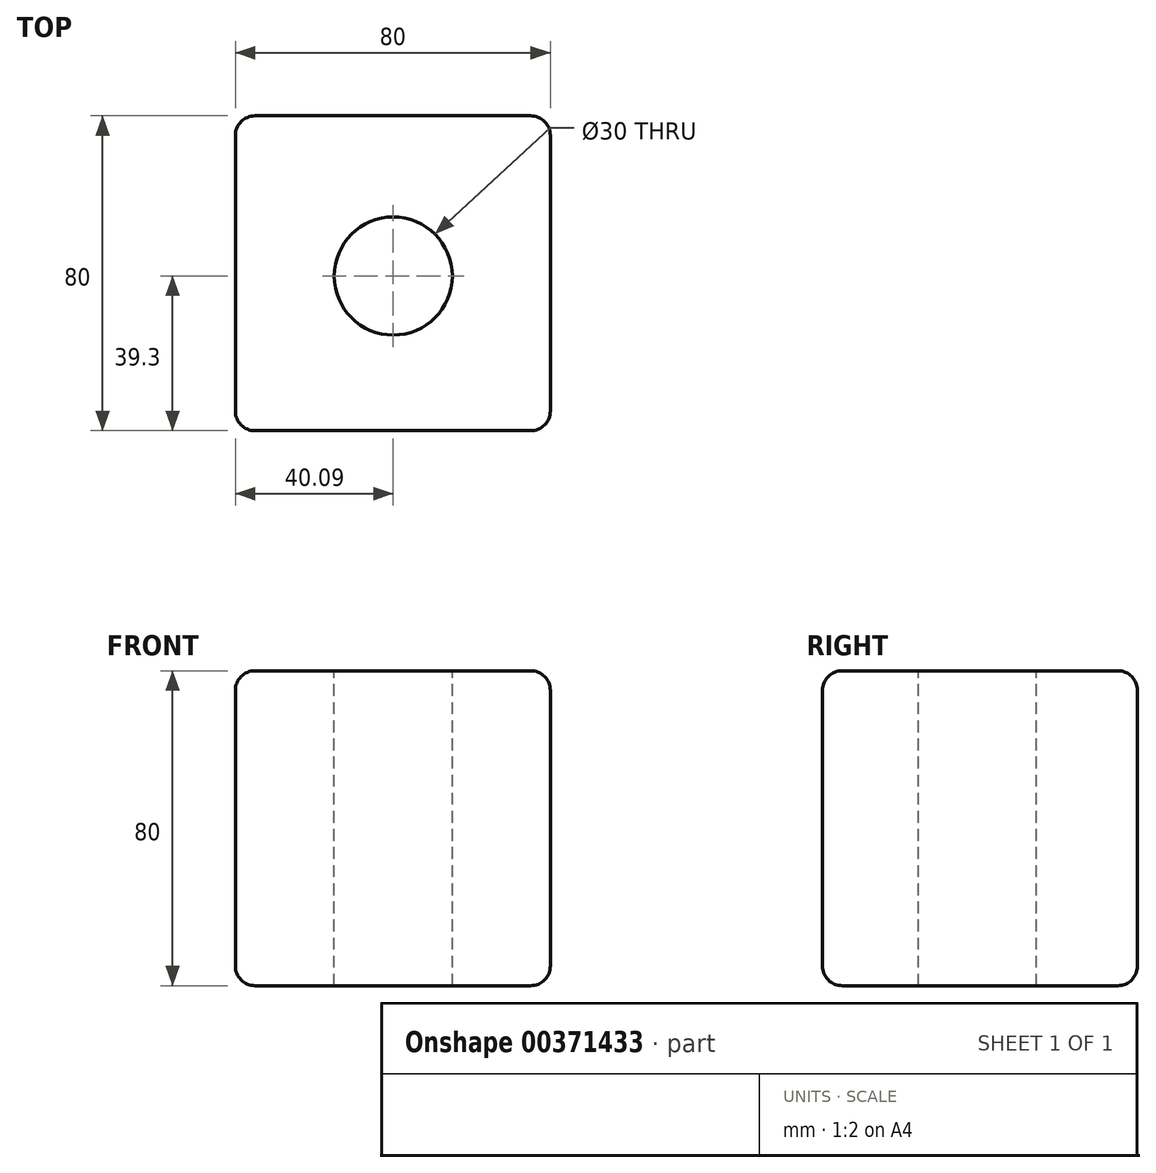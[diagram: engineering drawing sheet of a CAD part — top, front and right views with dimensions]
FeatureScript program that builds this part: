
annotation { "Feature Type Name" : "Feature", "Feature Type Description" : "" }
export const myFeature = defineFeature(function(context is Context, id is Id, definition is map)
    precondition{}
    {
        {
            var Q0;
            Q0=qCreatedBy(makeId("Top.planeOp"),FACE);
            var sketch = newSketch(context, id + "F0", { "sketchPlane" : qUnion([Q0])});
            skLineSegment(sketch, "E0.bottom", {"start": v(-46.4, 36.65) * mm, "end": v(33.6, 36.65) * mm});
            skLineSegment(sketch, "E0.top", {"start": v(-46.4, -43.35) * mm, "end": v(33.6, -43.35) * mm});
            skLineSegment(sketch, "E0.left", {"start": v(-46.4, 36.65) * mm, "end": v(-46.4, -43.35) * mm});
            skLineSegment(sketch, "E0.right", {"start": v(33.6, 36.65) * mm, "end": v(33.6, -43.35) * mm});
            skSolve(sketch);
        }
        {
            var Q0;
            Q0=makeQuery(id+"F0.imprint","IMPRINT",FACE,{"disambiguationData":[TD([[makeQuery(id+"F0.imprint","IMPRINT",EDGE,{"derivedFrom":sQuery(id+"F0.wireOp",EDGE,"E0.bottom")}),-1.0]])]});
            extrude(context, id + "F1", {"entities" : qUnion([Q0]), "depth" : 80 * mm});
        }
        {
            var Q0;
            Q0=makeQuery(id+"F1.opExtrude","CAP_FACE",FACE,{"disambiguationData":[OSD([sQuery(id+"F0.wireOp",EDGE,"E0.bottom"),sQuery(id+"F0.wireOp",EDGE,"E0.top"),sQuery(id+"F0.wireOp",EDGE,"E0.left"),sQuery(id+"F0.wireOp",EDGE,"E0.right")])],"isStart":false});
            var sketch = newSketch(context, id + "F2", { "sketchPlane" : qUnion([Q0])});
            skCircle(sketch, "E1", {"center": v(-6.3, -4.05) * mm, "radius": 15 * mm});
            skSolve(sketch);
        }
        {
            var Q0;
            Q0=makeQuery(id+"F2.imprint","IMPRINT",FACE,{"disambiguationData":[TD([[makeQuery(id+"F2.imprint","IMPRINT",EDGE,{"derivedFrom":sQuery(id+"F2.wireOp",EDGE,"E1")}),1.0]])]});
            extrude(context, id + "F3", {"entities" : qUnion([Q0]), "operationType" : NewBodyOperationType.REMOVE, "endBound" : BoundingType.THROUGH_ALL, "oppositeDirection" : true, "depth" : 25 * mm});
        }
        {
            var Q0;
            Q0=makeQuery(id+"F1.opExtrude","CAP_EDGE",EDGE,{"disambiguationData":[OSD([sQuery(id+"F0.wireOp",EDGE,"E0.bottom")])],"isStart":false});
            var Q1;
            Q1=makeQuery(id+"F1.opExtrude","CAP_EDGE",EDGE,{"disambiguationData":[OSD([sQuery(id+"F0.wireOp",EDGE,"E0.left")])],"isStart":false});
            var Q2;
            Q2=makeQuery(id+"F1.opExtrude","CAP_EDGE",EDGE,{"disambiguationData":[OSD([sQuery(id+"F0.wireOp",EDGE,"E0.top")])],"isStart":false});
            var Q3;
            Q3=makeQuery(id+"F1.opExtrude","CAP_EDGE",EDGE,{"disambiguationData":[OSD([sQuery(id+"F0.wireOp",EDGE,"E0.right")])],"isStart":false});
            var Q4;
            Q4=makeQuery(id+"F1.opExtrude","SWEPT_EDGE",EDGE,{"disambiguationData":[OSD([sQuery(id+"F0.wireOp",EDGE,"E0.bottom"),sQuery(id+"F0.wireOp",EDGE,"E0.right")])]});
            var Q5;
            Q5=makeQuery(id+"F1.opExtrude","SWEPT_FACE",FACE,{"disambiguationData":[OSD([sQuery(id+"F0.wireOp",EDGE,"E0.right")])]});
            var Q6;
            Q6=makeQuery(id+"F1.opExtrude","SWEPT_EDGE",EDGE,{"disambiguationData":[OSD([sQuery(id+"F0.wireOp",EDGE,"E0.bottom"),sQuery(id+"F0.wireOp",EDGE,"E0.left")])]});
            var Q7;
            Q7=makeQuery(id+"F1.opExtrude","SWEPT_FACE",FACE,{"disambiguationData":[OSD([sQuery(id+"F0.wireOp",EDGE,"E0.left")])]});
            var Q8;
            Q8=makeQuery(id+"F1.opExtrude","SWEPT_EDGE",EDGE,{"disambiguationData":[OSD([sQuery(id+"F0.wireOp",EDGE,"E0.top"),sQuery(id+"F0.wireOp",EDGE,"E0.left")])]});
            var Q9;
            Q9=makeQuery(id+"F1.opExtrude","CAP_EDGE",EDGE,{"disambiguationData":[OSD([sQuery(id+"F0.wireOp",EDGE,"E0.left")])],"isStart":true});
            var Q10;
            Q10=makeQuery(id+"F1.opExtrude","CAP_EDGE",EDGE,{"disambiguationData":[OSD([sQuery(id+"F0.wireOp",EDGE,"E0.bottom")])],"isStart":true});
            var Q11;
            Q11=makeQuery(id+"F1.opExtrude","CAP_EDGE",EDGE,{"disambiguationData":[OSD([sQuery(id+"F0.wireOp",EDGE,"E0.top")])],"isStart":true});
            fillet(context, id + "F4", {"entities" : qUnion([Q0, Q1, Q2, Q3, Q4, Q5, Q6, Q7, Q8, Q9, Q10, Q11]), "radius" : 5 * mm, "tangentPropagation" : true, "allowEdgeOverflow" : false});
        }
    });
